# Revit family: Camera-Security-HanhwaTechwin-Bullet-Wisenet X-XNO-6120R_mm
name_source: partatom
category: Security Devices
units: mm (PartAtom-declared; Revit-internal decimal feet)

## family parameters
Cut with Voids When Loaded = No
Host = Face
Maintain Annotation Orientation = No
OmniClass Number = 23.85.30.17.14
OmniClass Title = Video Surveillance
Part Type = Normal
Room Calculation Point = No
Round Connector Dimension = Use Diameter
Shared = No

## types (1)
- Standard
    Alarm Events = File Upload Via FTP, E-mail, Notification via e-mail, Local Storage (SD / SDHC /
SDXC) or NAS recording at event triggers, External output, Preset
    Alarm Input and Output = Input 1ea / Output 1ea
    Alarm Triggers = Alarm Input, Motion detection, Video & Audio Analytics, Network disconnect
    Application Programming Interface = ONVIF Profile S/G, SUNAPI 2.0 (HTTP API), Wisenet Open Platform
    AssetType = Fixed
    Audio Communication = Bi-directional (2-way)
    Audio Compression Format = G.711 u-law/G.726 Selectable, G.726 (ADPCM) 8KHz, G.711 8KHz
G.726 : 16Kbps, 24Kbps, 32Kbps, 40Kbps, AAC-LC : 48Kbps at 16KHz
    Audio In and Out = Selectable (Mic in / Line in), Supply Voltage : 2.5V DC (4mA), Input Impedance : Approx. 2K Ohm / Line Out (3.5mm Mono Jack), Max Output Level: 1 Vrms
    BIMObjectName = Role_Source_Type_GenericFaceBased
    Backlight Compensation = Off / BLC / HLC / WDR
    Bitrate Control Method = H.265 / H.264 : CBR or VBR, MJPEG : VBR
    Camera Title = Off / On (Displayed up to 85 Characters)
- W/W : English / Numeric / Special Characters
- China : English / Numeric / Special / Chinese Characters
- Common : Multi-line (Max. 5), Color (Grey / Green / Red / Blue / Black / White),
Transparency, Auto scale by Resolution
    Category = 2M Network IR Bullet Camera
    Central Management Software = SmartViewer
    Color = Dark gray
    Contrast = Level adjusment
    Contrast Enhancement = SSDR (Off / On)
    Day and Night = Auto (ICR) / Color / B/W / External / Schedule
    Default Elevation = 1219.2 mm  [stored 4 ft]
    Defog = Off / Auto / Manual
    Description = NBS standard template for generic face-based components
    Digital Image Stabilization = Off / On (Built-in Gyro sensor)
    Digital Noise Reduction = SSNRV (2D + 3D Noise filter) (Off / On)
    Edge Storage = SD / SDHC / SDXC 2Slot (Up to 512GB) - Continuous Recording (1st Slot to 2nd Slot)
- Motion Images recorded in the SD / SDHC / SDXC Memory Card Can be Downloaded.
NAS (Network Attached Storage), Local PC for Instant Recording
    Effective Pixels = 1,945(H) x 1,097(V) 2.13M
    Electronic Shutter Speed = Minimum / Maximum / Anti Flicker (2 ~ 1/12,000sec)
    Ethernet = RJ-45 (10/100BASE-T)
    Features = Max. 2Megapixel (1920 x 1080) resolution
• 5.2 ~ 62.4mm (Optical 12X) Optical Lens
• Max. 60fps@all resolutions (H.265 / H.264)
    Focal Length (Zoom Ratio) = 5.2 ~ 62.4mm (Optical 12X)
    Focus Control = Simple focus (Motorized V/F) / Manual, Remote control via network (Manual, Simple focus)
    Gain Control = Off / Low / Middle / High
    IP = IPv4, IPv6
    IR Viewable Length = 70m (229.66ft)
    Ingress Protection / Vandal Resistance = IP67, IP66, NEMA 4X / IK10
    Input Vooltage / Current = 24V AC, 12V DC, PoE (IEEE802.3af Class3)
    LDC (Lens Distortion Correction) = Off / On (5 Levels with Min / Max)
    Lens Type = DC auto iris, P-Iris
    Manufacturer = Hanwha Techwin
    ManufacturerName = HanwhaTechwin
    ManufacturerURL = http://security.hanwhatechwin.com
    Material = Aluminum
    Max. Aperture Ratio = F1.6(Wide) ~ F3.0(Tele)
    Maximum Framerate = H.265 / H.264 : Max. 60fps at all resolutions, MJPEG : Max. 30fps at all resolutions
    Megapixels = 2
    Min. Illumination = Color : 0.03 Lux (F1.6, 1/30sec), B/W : 0Lux (IR LED on)
    Min. Object Distance = 1.5m (4.92ft)
    Model = XNO-6120R
    ModelNumber = XNO-6120R
    ModelReference = HanwhaTechwin
    Motion Detection = Off / On (8ea, 8Point polygonal zones), Handover
    Mount Type = Board-in Type
    Name = XNO-6120R
    NominalLength = 368.6.mm (14.51")
    NominalWidth = Ø147.5 (Ø5.81")
    Operating Temperature / Humidity = -40°C ~ +55°C (-40°F ~ +131°F) / Less than 90% RH * Start up should be done at above -35°C (-31°F)
    Pixel Counter = Support
    Power Consumption = 24V AC : Max 14.5W, 12V DC : Max 12.5W, PoE : Max 12.95W
    Privacy Masking = Off / On (32ea, Rectangle zones) - Color : Grey / Green / Red / Blue / Black / White - Mosaic
    Product Documentation Link = https://www.hanwha-security.com
    Product Material = Aluminum - HanwhaTechwin - Dark Gray
    Protocol = TCP/IP, UDP/IP, RTP (UDP), RTP (TCP), RTCP,RTSP, NTP, HTTP, HTTPS, SSL/TLS, DHCP, PPPoE, FTP, SMTP,
ICMP, IGMP, SNMPv1/v2c/v3 (MIB-2), ARP, DNS, DDNS, QoS, PIM-SM, UPnP, Bonjour
    ReplacementCost = Ø147.5 (Ø5.81")
    Resolution = 1920 x 1080, 1280 x 1024, 1280 x 960, 1280 x 720, 1024 x 768, 800 x 600,
800 x 448, 720 x 576, 720 x 480, 640 x 480, 640 x 360, 320 x 240
    S / N Ratio = 50 dB
    Scanning System = Progressive
    Security = HTTPS (SSL) Login Authentication, Digest Login Authentication IP address filtering, User access log, 802.1X Authentication (EAP-TLS, EAP-LEAP)
    Shape = Bullet
    Size = Ø147.5 x 368.6.mm (Ø5.81" x 14.51") (Without sunshield)
    Smart Codec = Manual mode (Area-based : 5ea)
    Storage Temperature / Humidity = -50°C ~ +60°C (-58°F ~ +140°F) / Less than 90% RH
    Streaming Capability = Multiple streaming (Up to 10 profiles)
    Streaming Method = Unicast / Multicast
    Total Pixels = 1,945(H) x 1,109(V) 2.16M
    URL = https://www.hanwha-security.com
    Uniclass2 = Pr_60_75_05_22
    Version = 1
    Video & Audio Analytics = Tampering, Loitering, Directional detection, Defocus Detection, Fog Detection,
Virtual Line, Enter / Exit, (Dis)Appear, Audio detection, Face detection, Motion
detection, Sound Classification
    Video Compression Format = H.265 / H.264 (MPEG-4 part 10/AVC) : Main / Baseline / High, MJPEG
    Video Out = CVBS : 1.0 Vp-p / 75Ω Composite, 720 x 480(N), 720 x 576(P), for Installation
USB : Micro USB Type B, 1280 x 720, for Installation
    Video Quality Adjustment = H.265 / H.264 : MJPEG : Target bitrate level control
    Voltage AC = 24V
    Voltage DC = 12V
    WarrantyDurationUnit = year
    Web Viewer = Supported OS : Windows 7, 8.1, 10, Mac OS X 10.10. 10.11 10.12
Non-Plugin Web Viewer
Supported Browser : Google Chrome 56, MS Edge 39, Mozilla Firefox 49
(Window 64bit only), Apple Safari 10 (Mac OS X only)
Plug-in Web Viewer
Supported Browser : MS Explore 11, Apple Safari 10 (Mac OS X only)
    Webpage Language = English, Korean, Chinese, French, Italian, Spanish, German, Japanese,
Russian, Swedish, Portuguese, Czech, Polish, Turkish, Dutch, Hungarian, Greek
    Weight = 0.995Kg (2.19lb)
    White Balance = ATW / AWC / Manual / Indoor / Outdoor (Included Mercury & Sodium)
    Wide Dynamic Range = 150 dB
    WiseStreamII = Support

note: [stored X ft] marks values corroborated as IEEE doubles in the binary element streams (Revit-internal decimal feet)

## geometry (parser evidence)
native form markers: Sweep x9
no freeform markers — native parametric forms only
